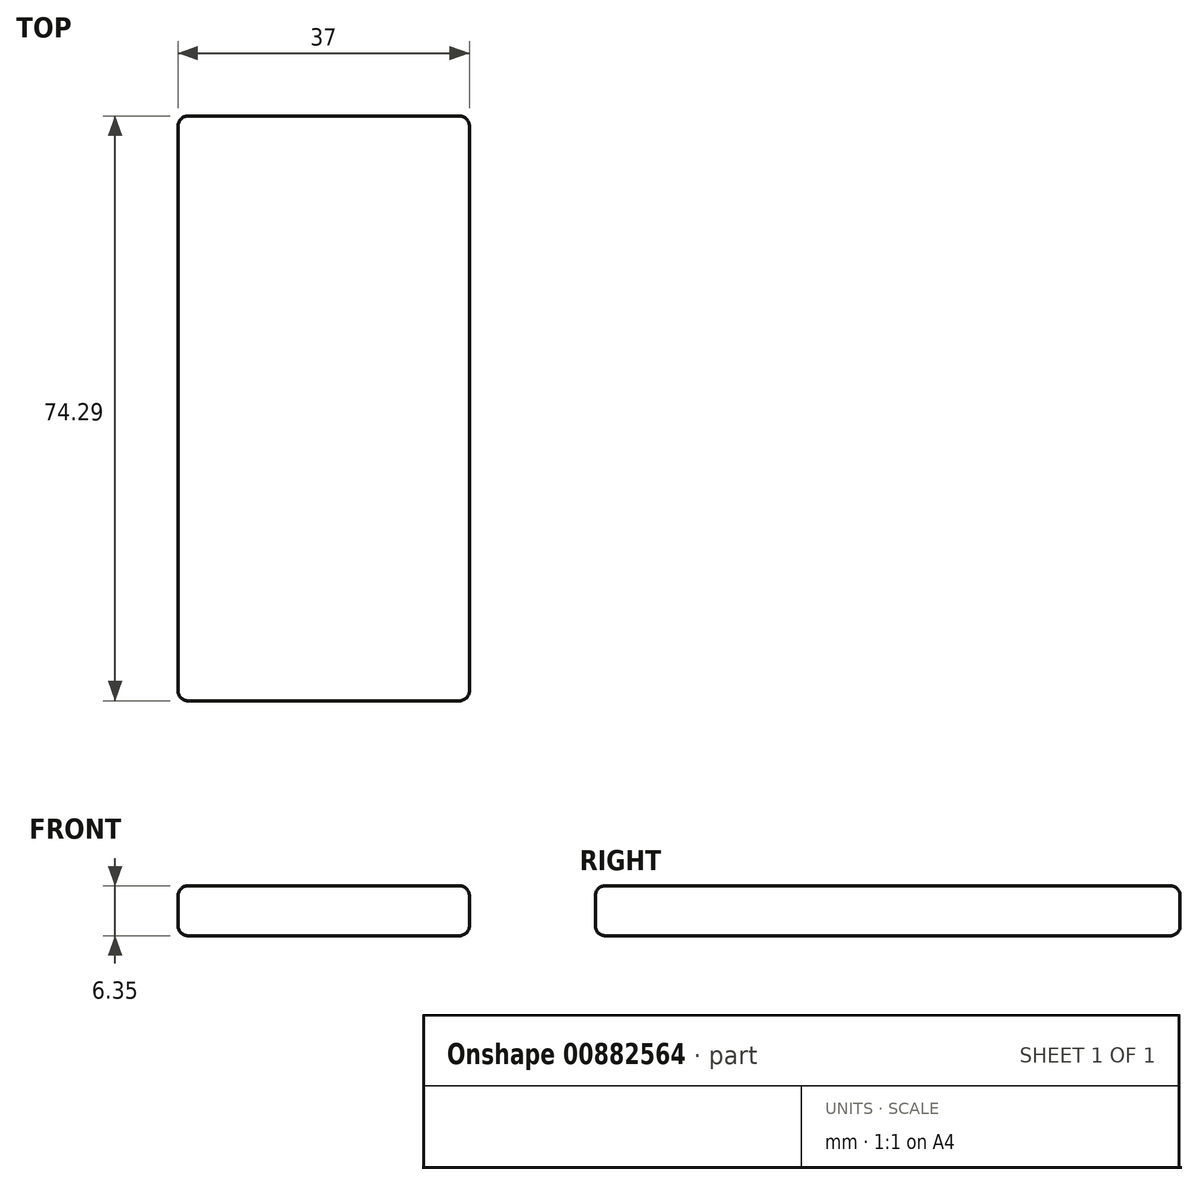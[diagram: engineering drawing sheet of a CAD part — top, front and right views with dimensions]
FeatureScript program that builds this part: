
annotation { "Feature Type Name" : "Feature", "Feature Type Description" : "" }
export const myFeature = defineFeature(function(context is Context, id is Id, definition is map)
    precondition{}
    {
        {
            var Q0;
            Q0=qCreatedBy(makeId("Top.planeOp"),FACE);
            var sketch = newSketch(context, id + "F0", { "sketchPlane" : qUnion([Q0])});
            skLineSegment(sketch, "E0.bottom", {"start": v(0, 0) * mm, "end": v(-37, 0) * mm});
            skLineSegment(sketch, "E0.top", {"start": v(0, -74.29) * mm, "end": v(-37, -74.29) * mm});
            skLineSegment(sketch, "E0.left", {"start": v(0, 0) * mm, "end": v(0, -74.29) * mm});
            skLineSegment(sketch, "E0.right", {"start": v(-37, 0) * mm, "end": v(-37, -74.29) * mm});
            skSolve(sketch);
        }
        {
            var Q0;
            Q0=makeQuery(id+"F0.imprint","IMPRINT",FACE,{"disambiguationData":[TD([[makeQuery(id+"F0.imprint","IMPRINT",EDGE,{"derivedFrom":sQuery(id+"F0.wireOp",EDGE,"E0.bottom")}),1.0]])]});
            extrude(context, id + "F1", {"entities" : qUnion([Q0]), "depth" : 6.35 * mm, "offsetDistance" : 25.4 * mm});
        }
        {
            var Q0;
            Q0=makeQuery(id+"F1.opExtrude","CAP_EDGE",EDGE,{"disambiguationData":[OSD([sQuery(id+"F0.wireOp",EDGE,"E0.left")])],"isStart":false});
            var Q1;
            Q1=makeQuery(id+"F1.opExtrude","CAP_EDGE",EDGE,{"disambiguationData":[OSD([sQuery(id+"F0.wireOp",EDGE,"E0.top")])],"isStart":false});
            var Q2;
            Q2=makeQuery(id+"F1.opExtrude","CAP_EDGE",EDGE,{"disambiguationData":[OSD([sQuery(id+"F0.wireOp",EDGE,"E0.right")])],"isStart":false});
            var Q3;
            Q3=makeQuery(id+"F1.opExtrude","CAP_EDGE",EDGE,{"disambiguationData":[OSD([sQuery(id+"F0.wireOp",EDGE,"E0.bottom")])],"isStart":false});
            var Q4;
            Q4=makeQuery(id+"F1.opExtrude","CAP_EDGE",EDGE,{"disambiguationData":[OSD([sQuery(id+"F0.wireOp",EDGE,"E0.left")])],"isStart":true});
            var Q5;
            Q5=makeQuery(id+"F1.opExtrude","CAP_EDGE",EDGE,{"disambiguationData":[OSD([sQuery(id+"F0.wireOp",EDGE,"E0.bottom")])],"isStart":true});
            var Q6;
            Q6=makeQuery(id+"F1.opExtrude","SWEPT_EDGE",EDGE,{"disambiguationData":[OSD([sQuery(id+"F0.wireOp",EDGE,"E0.bottom"),sQuery(id+"F0.wireOp",EDGE,"E0.right")])]});
            var Q7;
            Q7=makeQuery(id+"F1.opExtrude","SWEPT_FACE",FACE,{"disambiguationData":[OSD([sQuery(id+"F0.wireOp",EDGE,"E0.right")])]});
            var Q8;
            Q8=makeQuery(id+"F1.opExtrude","SWEPT_EDGE",EDGE,{"disambiguationData":[OSD([sQuery(id+"F0.wireOp",EDGE,"E0.top"),sQuery(id+"F0.wireOp",EDGE,"E0.right")])]});
            var Q9;
            Q9=makeQuery(id+"F1.opExtrude","CAP_EDGE",EDGE,{"disambiguationData":[OSD([sQuery(id+"F0.wireOp",EDGE,"E0.top")])],"isStart":true});
            var Q10;
            Q10=makeQuery(id+"F1.opExtrude","CAP_EDGE",EDGE,{"disambiguationData":[OSD([sQuery(id+"F0.wireOp",EDGE,"E0.right")])],"isStart":true});
            var Q11;
            Q11=makeQuery(id+"F1.opExtrude","SWEPT_EDGE",EDGE,{"disambiguationData":[OSD([sQuery(id+"F0.wireOp",EDGE,"E0.top"),sQuery(id+"F0.wireOp",EDGE,"E0.left")])]});
            var Q12;
            Q12=makeQuery(id+"F1.opExtrude","SWEPT_EDGE",EDGE,{"disambiguationData":[OSD([sQuery(id+"F0.wireOp",EDGE,"E0.bottom"),sQuery(id+"F0.wireOp",EDGE,"E0.left")])]});
            fillet(context, id + "F2", {"entities" : qUnion([Q0, Q1, Q2, Q3, Q4, Q5, Q6, Q7, Q8, Q9, Q10, Q11, Q12]), "radius" : 1.27 * mm, "tangentPropagation" : true, "allowEdgeOverflow" : false});
        }
    });
